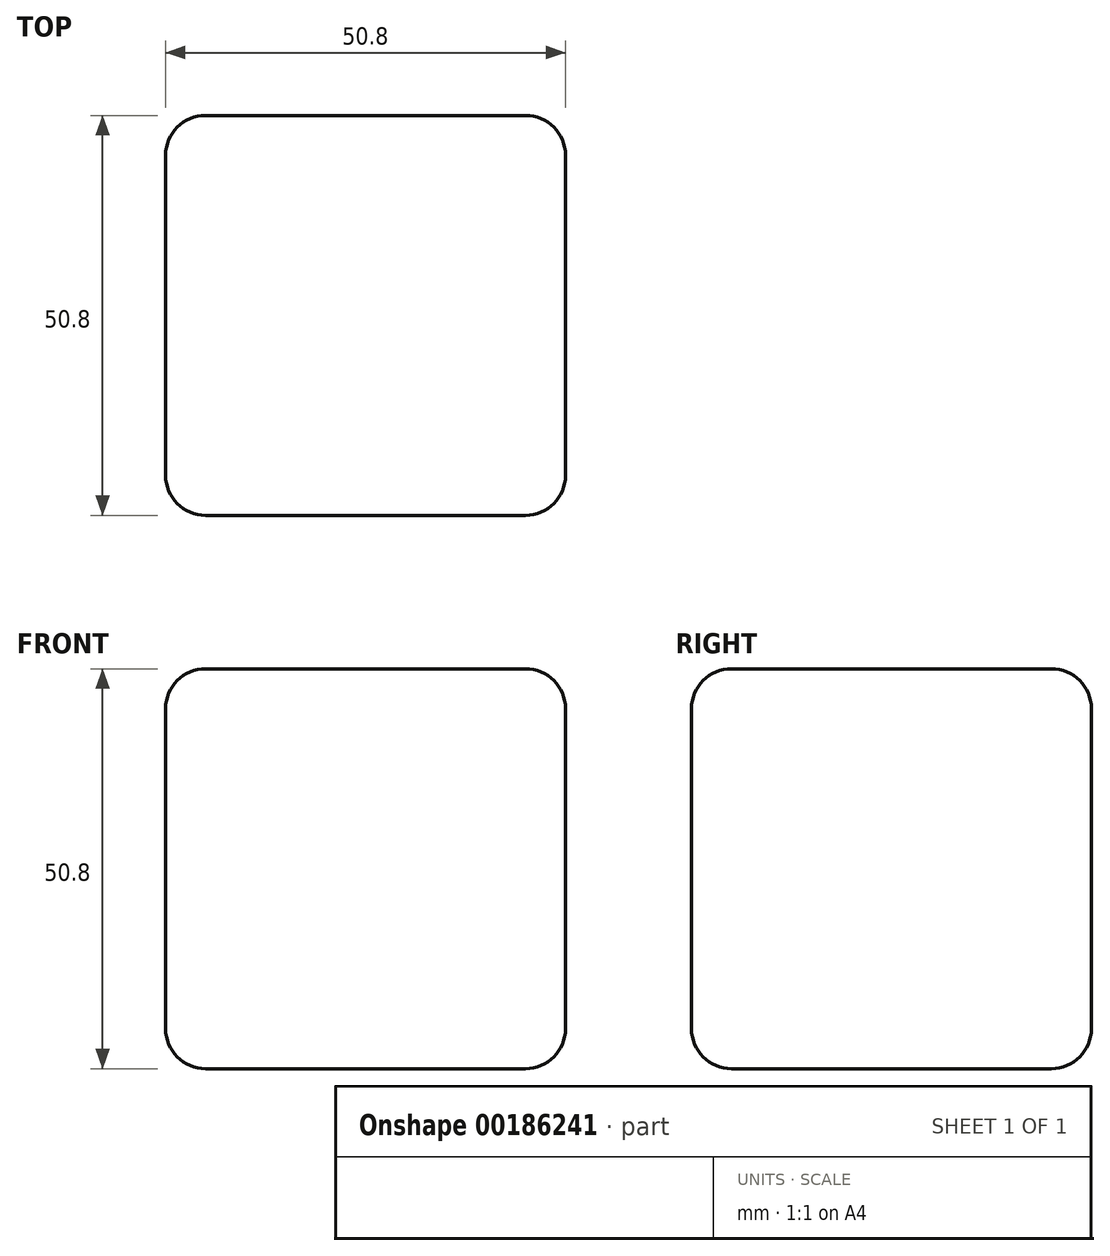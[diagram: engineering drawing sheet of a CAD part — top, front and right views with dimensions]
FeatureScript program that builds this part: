
annotation { "Feature Type Name" : "Feature", "Feature Type Description" : "" }
export const myFeature = defineFeature(function(context is Context, id is Id, definition is map)
    precondition{}
    {
        {
            var Q0;
            Q0=qCreatedBy(makeId("Top.planeOp"),FACE);
            var sketch = newSketch(context, id + "F0", { "sketchPlane" : qUnion([Q0])});
            skLineSegment(sketch, "E0.bottom", {"start": v(-25.4, -25.4) * mm, "end": v(25.4, -25.4) * mm});
            skLineSegment(sketch, "E0.top", {"start": v(-25.4, 25.4) * mm, "end": v(25.4, 25.4) * mm});
            skLineSegment(sketch, "E0.left", {"start": v(-25.4, -25.4) * mm, "end": v(-25.4, 25.4) * mm});
            skLineSegment(sketch, "E0.right", {"start": v(25.4, -25.4) * mm, "end": v(25.4, 25.4) * mm});
            skPoint(sketch, "E0.middle", {"position": v(0, 0) * mm});
            skSolve(sketch);
        }
        {
            var Q0;
            Q0 = qSketchRegion(id + "F0", true);
            extrude(context, id + "F1", {"entities" : qUnion([Q0]), "depth" : 50.8 * mm});
        }
        {
            var Q0;
            Q0=makeQuery(id+"F1.opExtrude","SWEPT_FACE",FACE,{"disambiguationData":[OSD([sQuery(id+"F0.wireOp",EDGE,"E0.bottom")])]});
            var Q1;
            Q1=makeQuery(id+"F1.opExtrude","CAP_FACE",FACE,{"disambiguationData":[OSD([sQuery(id+"F0.wireOp",EDGE,"E0.bottom"),sQuery(id+"F0.wireOp",EDGE,"E0.top"),sQuery(id+"F0.wireOp",EDGE,"E0.left"),sQuery(id+"F0.wireOp",EDGE,"E0.right")])],"isStart":false});
            var Q2;
            Q2=makeQuery(id+"F1.opExtrude","SWEPT_FACE",FACE,{"disambiguationData":[OSD([sQuery(id+"F0.wireOp",EDGE,"E0.right")])]});
            var Q3;
            Q3=makeQuery(id+"F1.opExtrude","SWEPT_FACE",FACE,{"disambiguationData":[OSD([sQuery(id+"F0.wireOp",EDGE,"E0.left")])]});
            var Q4;
            Q4=makeQuery(id+"F1.opExtrude","SWEPT_FACE",FACE,{"disambiguationData":[OSD([sQuery(id+"F0.wireOp",EDGE,"E0.top")])]});
            fillet(context, id + "F2", {"entities" : qUnion([Q0, Q1, Q2, Q3, Q4]), "radius" : 5.08 * mm, "tangentPropagation" : true, "allowEdgeOverflow" : false});
        }
    });
